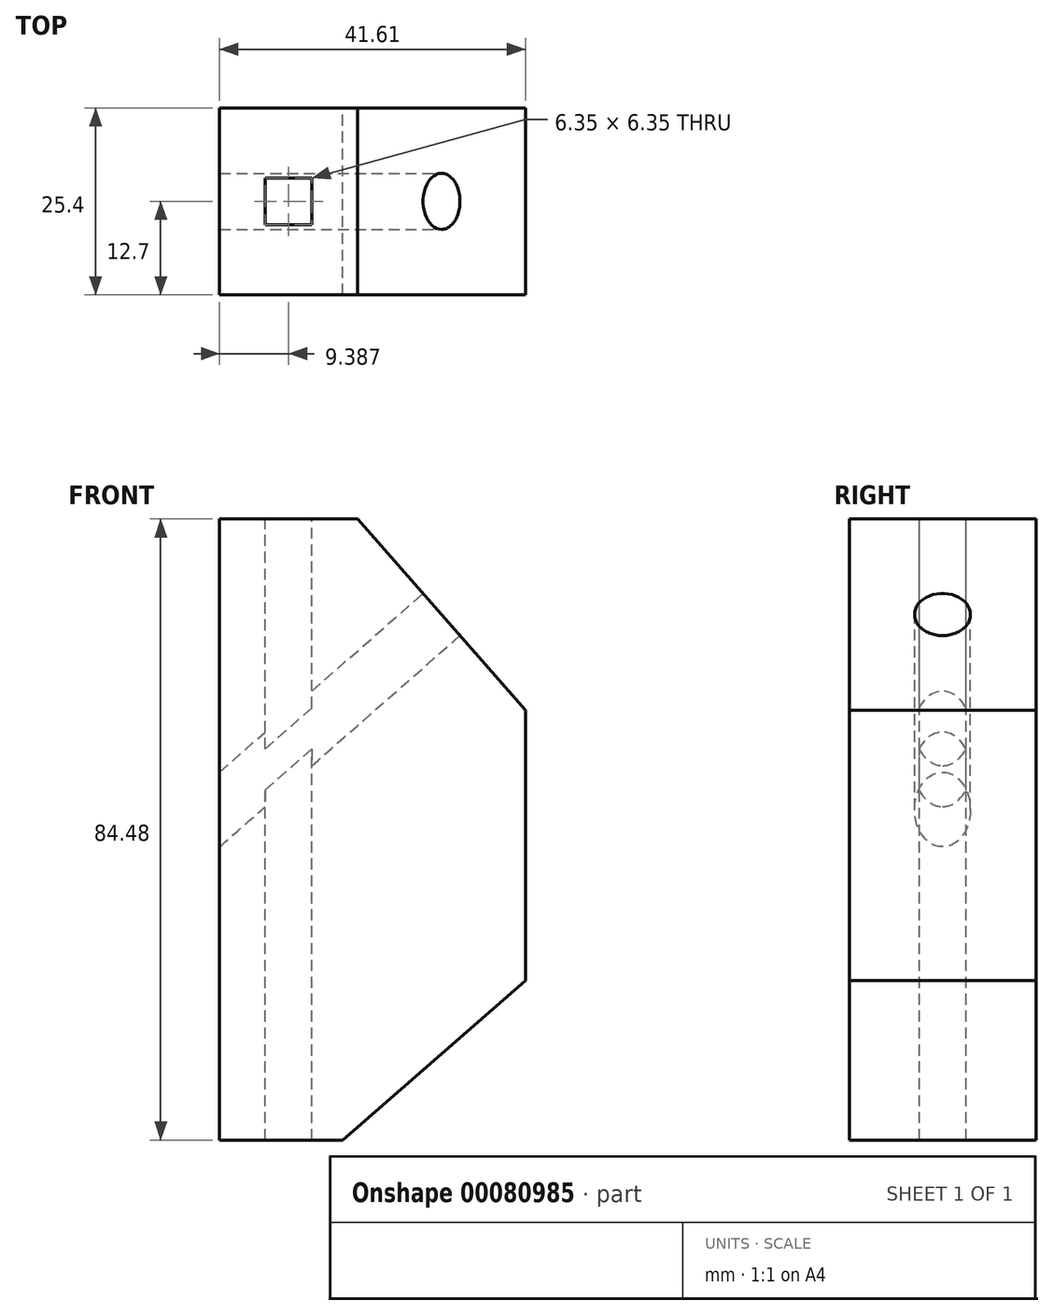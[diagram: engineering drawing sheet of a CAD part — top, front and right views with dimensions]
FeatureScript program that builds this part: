
annotation { "Feature Type Name" : "Feature", "Feature Type Description" : "" }
export const myFeature = defineFeature(function(context is Context, id is Id, definition is map)
    precondition{}
    {
        {
            var Q0;
            Q0=qCreatedBy(makeId("Front.planeOp"),FACE);
            var sketch = newSketch(context, id + "F0", { "sketchPlane" : qUnion([Q0])});
            skLineSegment(sketch, "E0", {"start": v(0, 0) * mm, "end": v(0, 45.33) * mm});
            skLineSegment(sketch, "E1", {"start": v(0, 45.33) * mm, "end": v(18.77, 45.33) * mm});
            skLineSegment(sketch, "E2", {"start": v(18.77, 45.33) * mm, "end": v(41.61, 19.34) * mm});
            skLineSegment(sketch, "E3", {"start": v(41.61, 19.34) * mm, "end": v(41.61, -17.43) * mm});
            skLineSegment(sketch, "E4", {"start": v(41.61, -17.43) * mm, "end": v(16.73, -39.15) * mm});
            skLineSegment(sketch, "E5", {"start": v(16.73, -39.15) * mm, "end": v(0, -39.15) * mm});
            skLineSegment(sketch, "E6", {"start": v(0, -39.15) * mm, "end": v(0, 0) * mm});
            skSolve(sketch);
        }
        {
            var Q0;
            Q0=makeQuery(id+"F0.imprint","IMPRINT",FACE,{"disambiguationData":[TD([[makeQuery(id+"F0.imprint","IMPRINT",EDGE,{"derivedFrom":sQuery(id+"F0.wireOp",EDGE,"E0")}),-1.0]])]});
            extrude(context, id + "F1", {"entities" : qUnion([Q0]), "depth" : 25.4 * mm});
        }
        {
            var Q0;
            Q0=makeQuery(id+"F1.opExtrude","SWEPT_FACE",FACE,{"disambiguationData":[OSD([sQuery(id+"F0.wireOp",EDGE,"E2")])]});
            var sketch = newSketch(context, id + "F2", { "sketchPlane" : qUnion([Q0])});
            skCircle(sketch, "E7", {"center": v(-12.7, 4.36) * mm, "radius": 3.81 * mm});
            skPoint(sketch, "E7.centerSnap0", {"position": v(-12.7, 21.66) * mm});
            skPoint(sketch, "E7.centerSnap1", {"position": v(0, 4.36) * mm});
            skSolve(sketch);
        }
        {
            var Q0;
            Q0=makeQuery(id+"F2.imprint","IMPRINT",FACE,{"disambiguationData":[TD([[makeQuery(id+"F2.imprint","IMPRINT",EDGE,{"derivedFrom":sQuery(id+"F2.wireOp",EDGE,"E7")}),1.0]])]});
            var Q1;
            Q1=sQuery(id+"F2.wireOp",EDGE,"E7");
            extrude(context, id + "F3", {"entities" : qUnion([Q0]), "operationType" : NewBodyOperationType.REMOVE, "surfaceEntities" : qUnion([Q1]), "endBound" : BoundingType.THROUGH_ALL, "oppositeDirection" : true, "depth" : 25.4 * mm});
        }
        {
            var Q0;
            Q0=makeQuery(id+"F1.opExtrude","SWEPT_FACE",FACE,{"disambiguationData":[OSD([sQuery(id+"F0.wireOp",EDGE,"E1")])]});
            var sketch = newSketch(context, id + "F4", { "sketchPlane" : qUnion([Q0])});
            skLineSegment(sketch, "E8.bottom", {"start": v(6.21, -15.88) * mm, "end": v(12.56, -15.88) * mm});
            skLineSegment(sketch, "E8.top", {"start": v(6.21, -9.53) * mm, "end": v(12.56, -9.53) * mm});
            skLineSegment(sketch, "E8.left", {"start": v(6.21, -15.88) * mm, "end": v(6.21, -9.53) * mm});
            skLineSegment(sketch, "E8.right", {"start": v(12.56, -15.88) * mm, "end": v(12.56, -9.53) * mm});
            skLineSegment(sketch, "E9", {"start": v(0, -12.7) * mm, "end": v(18.77, -12.7) * mm});
            skLineSegment(sketch, "E10", {"start": v(9.39, -25.4) * mm, "end": v(9.39, 0) * mm});
            skPoint(sketch, "E11", {"position": v(6.21, -12.7) * mm});
            skPoint(sketch, "E12", {"position": v(9.39, -15.88) * mm});
            skSolve(sketch);
        }
        {
            var Q0;
            {var subQ0=sQuery(id+"F4.wireOp",EDGE,"E8.left");var subQ1=sQuery(id+"F4.wireOp",EDGE,"E8.bottom");var subQ2=makeQuery(id+"F4.imprint","INTERSECT",VERTEX,{"derivedFrom":[subQ1,subQ0]});Q0=makeQuery(id+"F4.imprint","IMPRINT",FACE,{"disambiguationData":[TD([[makeQuery(id+"F4.imprint","IMPRINT",EDGE,{"disambiguationData":[TD([[subQ2,-1.0]])],"derivedFrom":subQ1}),1.0]])]});}
            var Q1;
            {var subQ0=sQuery(id+"F4.wireOp",EDGE,"E8.left");var subQ1=sQuery(id+"F4.wireOp",EDGE,"E8.top");var subQ2=makeQuery(id+"F4.imprint","INTERSECT",VERTEX,{"derivedFrom":[subQ1,subQ0]});Q1=makeQuery(id+"F4.imprint","IMPRINT",FACE,{"disambiguationData":[TD([[makeQuery(id+"F4.imprint","IMPRINT",EDGE,{"disambiguationData":[TD([[subQ2,-1.0]])],"derivedFrom":subQ1}),-1.0]])]});}
            var Q2;
            {var subQ0=sQuery(id+"F4.wireOp",EDGE,"E8.right");var subQ1=sQuery(id+"F4.wireOp",EDGE,"E8.top");var subQ2=makeQuery(id+"F4.imprint","INTERSECT",VERTEX,{"derivedFrom":[subQ1,subQ0]});Q2=makeQuery(id+"F4.imprint","IMPRINT",FACE,{"disambiguationData":[TD([[makeQuery(id+"F4.imprint","IMPRINT",EDGE,{"disambiguationData":[TD([[subQ2,1.0]])],"derivedFrom":subQ1}),-1.0]])]});}
            var Q3;
            {var subQ0=sQuery(id+"F4.wireOp",EDGE,"E8.right");var subQ1=sQuery(id+"F4.wireOp",EDGE,"E8.bottom");var subQ2=makeQuery(id+"F4.imprint","INTERSECT",VERTEX,{"derivedFrom":[subQ1,subQ0]});Q3=makeQuery(id+"F4.imprint","IMPRINT",FACE,{"disambiguationData":[TD([[makeQuery(id+"F4.imprint","IMPRINT",EDGE,{"disambiguationData":[TD([[subQ2,1.0]])],"derivedFrom":subQ1}),1.0]])]});}
            extrude(context, id + "F5", {"entities" : qUnion([Q0, Q1, Q2, Q3]), "operationType" : NewBodyOperationType.REMOVE, "endBound" : BoundingType.THROUGH_ALL, "oppositeDirection" : true, "depth" : 25.4 * mm});
        }
    });
